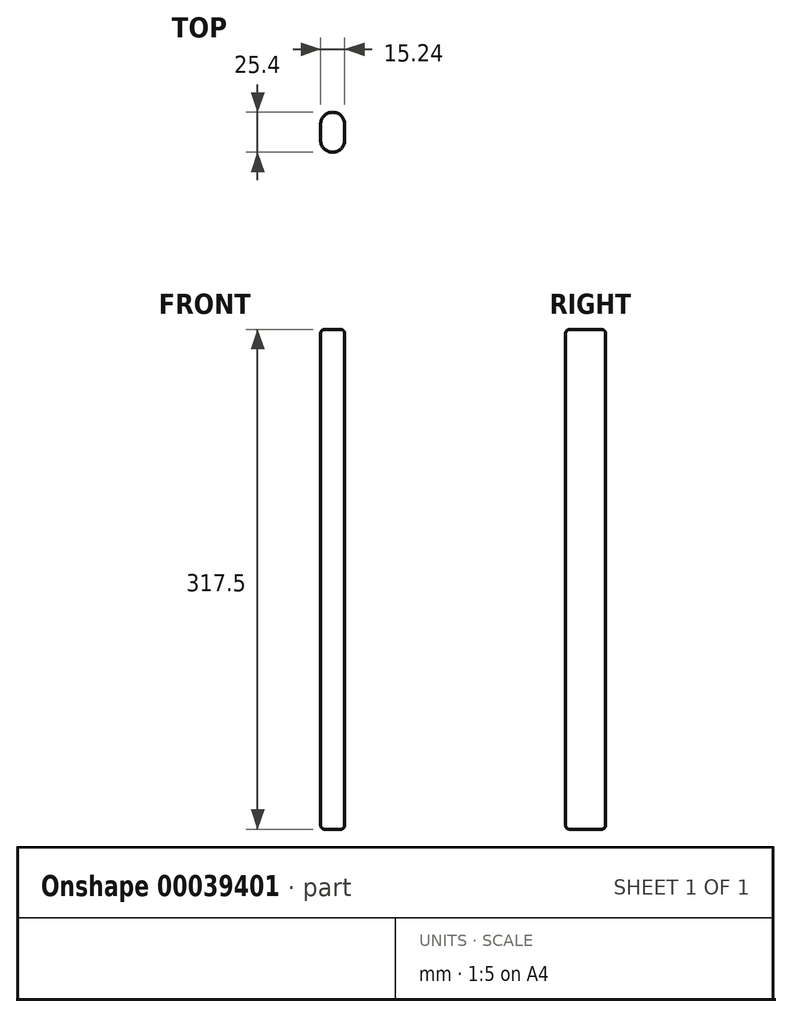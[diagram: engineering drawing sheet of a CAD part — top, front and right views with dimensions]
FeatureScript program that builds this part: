
annotation { "Feature Type Name" : "Feature", "Feature Type Description" : "" }
export const myFeature = defineFeature(function(context is Context, id is Id, definition is map)
    precondition{}
    {
        {
            var Q0;
            Q0=qCreatedBy(makeId("Top.planeOp"),FACE);
            var sketch = newSketch(context, id + "F0", { "sketchPlane" : qUnion([Q0])});
            skLineSegment(sketch, "E0", {"start": v(0, 0) * mm, "end": v(7.18, 0) * mm, "construction": true});
            skLineSegment(sketch, "E1", {"start": v(0, 0) * mm, "end": v(-8.06, 0) * mm, "construction": true});
            skLineSegment(sketch, "E2", {"start": v(-8.06, 0) * mm, "end": v(-8.06, -2.7) * mm});
            skLineSegment(sketch, "E3", {"start": v(-8.06, -2.7) * mm, "end": v(7.18, -2.7) * mm, "construction": true});
            skLineSegment(sketch, "E4", {"start": v(7.18, -2.7) * mm, "end": v(7.18, 0) * mm});
            skLineSegment(sketch, "E5", {"start": v(7.18, 0) * mm, "end": v(7.18, 7.45) * mm});
            skLineSegment(sketch, "E6", {"start": v(7.18, 7.45) * mm, "end": v(-8.06, 7.45) * mm, "construction": true});
            skLineSegment(sketch, "E7", {"start": v(-8.06, 7.45) * mm, "end": v(-8.06, 0) * mm});
            skArc(sketch, "E8", {"start": v(7.18, 7.45) * mm, "mid": v(-0.44, 15.07) * mm, "end": v(-8.06, 7.45) * mm});
            skArc(sketch, "E9", {"start": v(-8.06, -2.7) * mm, "mid": v(-0.44, -10.33) * mm, "end": v(7.18, -2.7) * mm});
            skSolve(sketch);
        }
        {
            var Q0;
            Q0=makeQuery(id+"F0.imprint","IMPRINT",FACE,{"disambiguationData":[TD([[makeQuery(id+"F0.imprint","IMPRINT",EDGE,{"derivedFrom":sQuery(id+"F0.wireOp",EDGE,"E2")}),1.0]])]});
            extrude(context, id + "F1", {"entities" : qUnion([Q0]), "depth" : 317.5 * mm});
        }
        {
            var Q0;
            Q0=makeQuery(id+"F1.opExtrude","CAP_EDGE",EDGE,{"disambiguationData":[OSD([sQuery(id+"F0.wireOp",EDGE,"E8")])],"isStart":false});
            var Q1;
            Q1=makeQuery(id+"F1.opExtrude","CAP_EDGE",EDGE,{"disambiguationData":[OSD([sQuery(id+"F0.wireOp",EDGE,"E4"),sQuery(id+"F0.wireOp",EDGE,"E5")])],"isStart":false});
            var Q2;
            Q2=makeQuery(id+"F1.opExtrude","CAP_EDGE",EDGE,{"disambiguationData":[OSD([sQuery(id+"F0.wireOp",EDGE,"E9")])],"isStart":false});
            var Q3;
            Q3=makeQuery(id+"F1.opExtrude","CAP_EDGE",EDGE,{"disambiguationData":[OSD([sQuery(id+"F0.wireOp",EDGE,"E2"),sQuery(id+"F0.wireOp",EDGE,"E7")])],"isStart":false});
            fillet(context, id + "F2", {"entities" : qUnion([Q0, Q1, Q2, Q3]), "radius" : 2.54 * mm, "tangentPropagation" : true, "allowEdgeOverflow" : false});
        }
        {
            var Q0;
            Q0=makeQuery(id+"F1.opExtrude","CAP_EDGE",EDGE,{"disambiguationData":[OSD([sQuery(id+"F0.wireOp",EDGE,"E8")])],"isStart":true});
            var Q1;
            Q1=makeQuery(id+"F1.opExtrude","CAP_EDGE",EDGE,{"disambiguationData":[OSD([sQuery(id+"F0.wireOp",EDGE,"E9")])],"isStart":true});
            var Q2;
            Q2=makeQuery(id+"F1.opExtrude","CAP_EDGE",EDGE,{"disambiguationData":[OSD([sQuery(id+"F0.wireOp",EDGE,"E4"),sQuery(id+"F0.wireOp",EDGE,"E5")])],"isStart":true});
            var Q3;
            Q3=makeQuery(id+"F1.opExtrude","CAP_EDGE",EDGE,{"disambiguationData":[OSD([sQuery(id+"F0.wireOp",EDGE,"E2"),sQuery(id+"F0.wireOp",EDGE,"E7")])],"isStart":true});
            fillet(context, id + "F3", {"entities" : qUnion([Q0, Q1, Q2, Q3]), "radius" : 2.54 * mm, "tangentPropagation" : true, "allowEdgeOverflow" : false});
        }
    });
